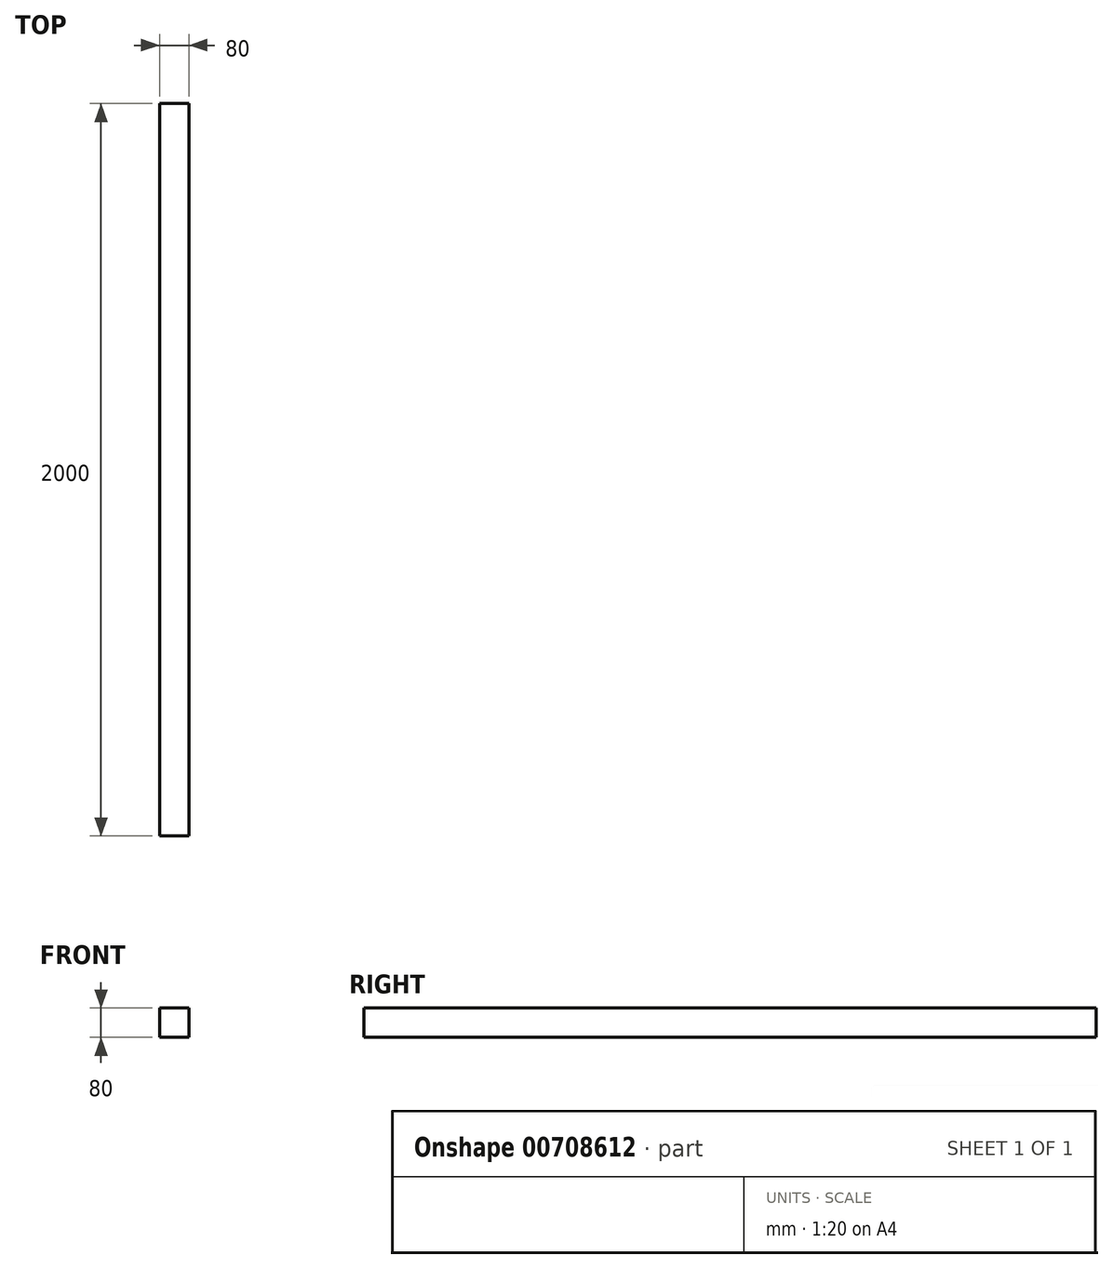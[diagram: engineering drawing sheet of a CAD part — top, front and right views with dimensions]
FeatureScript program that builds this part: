
annotation { "Feature Type Name" : "Feature", "Feature Type Description" : "" }
export const myFeature = defineFeature(function(context is Context, id is Id, definition is map)
    precondition{}
    {
        {
            var Q0;
            Q0=qCreatedBy(makeId("Front.planeOp"),FACE);
            var sketch = newSketch(context, id + "F0", { "sketchPlane" : qUnion([Q0])});
            skLineSegment(sketch, "E0.bottom", {"start": v(40, 40) * mm, "end": v(-40, 40) * mm});
            skLineSegment(sketch, "E0.top", {"start": v(40, -40) * mm, "end": v(-40, -40) * mm});
            skLineSegment(sketch, "E0.left", {"start": v(40, 40) * mm, "end": v(40, -40) * mm});
            skLineSegment(sketch, "E0.right", {"start": v(-40, 40) * mm, "end": v(-40, -40) * mm});
            skPoint(sketch, "E0.middle", {"position": v(0, 0) * mm});
            skSolve(sketch);
        }
        {
            var Q0;
            Q0=makeQuery(id+"F0.imprint","IMPRINT",FACE,{"disambiguationData":[TD([[makeQuery(id+"F0.imprint","IMPRINT",EDGE,{"derivedFrom":sQuery(id+"F0.wireOp",EDGE,"E0.bottom")}),1.0]])]});
            extrude(context, id + "F1", {"entities" : qUnion([Q0]), "depth" : 2000 * mm, "offsetDistance" : 25 * mm});
        }
    });
